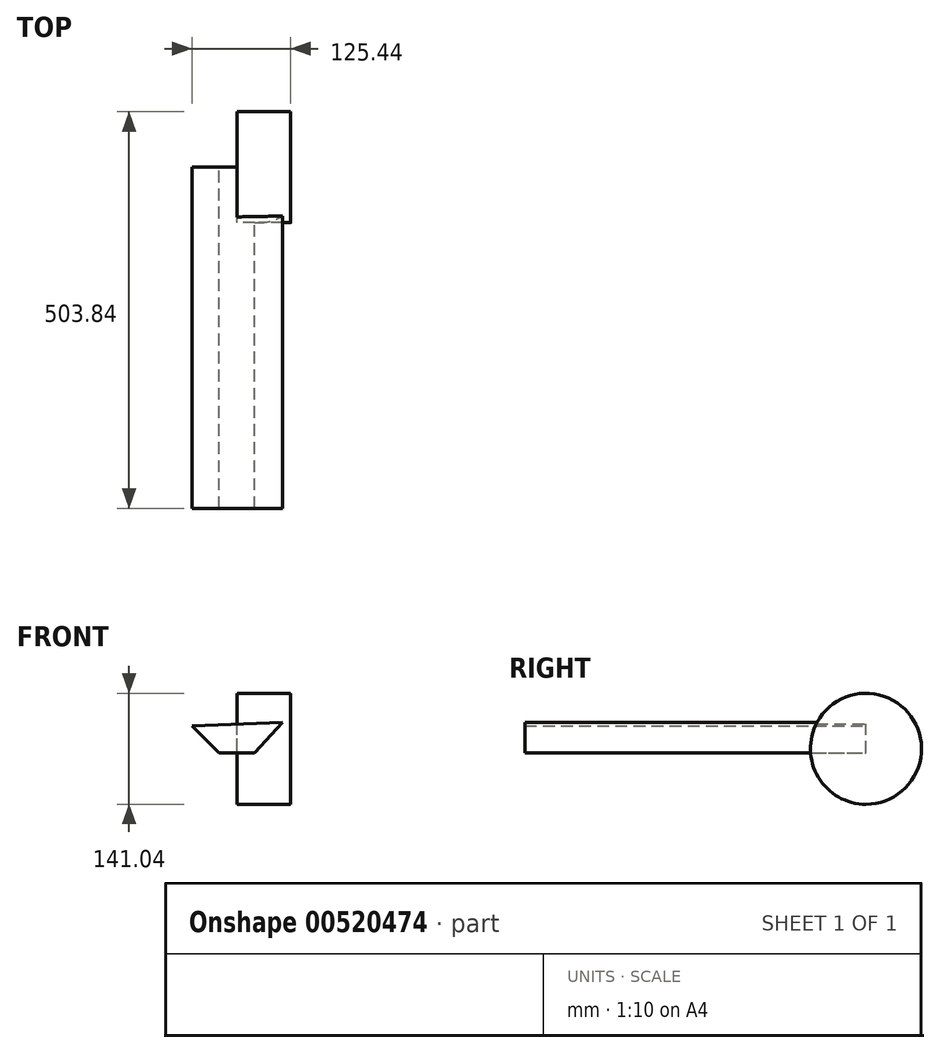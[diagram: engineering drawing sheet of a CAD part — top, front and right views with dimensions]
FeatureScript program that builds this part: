
annotation { "Feature Type Name" : "Feature", "Feature Type Description" : "" }
export const myFeature = defineFeature(function(context is Context, id is Id, definition is map)
    precondition{}
    {
        {
            var Q0;
            Q0=qCreatedBy(makeId("Front.planeOp"),FACE);
            var sketch = newSketch(context, id + "F0", { "sketchPlane" : qUnion([Q0])});
            skLineSegment(sketch, "E0", {"start": v(-23, 1.23) * mm, "end": v(22.4, 1.23) * mm});
            skLineSegment(sketch, "E1", {"start": v(22.4, 1.23) * mm, "end": v(57.98, 39.88) * mm});
            skLineSegment(sketch, "E2", {"start": v(57.98, 39.88) * mm, "end": v(22.4, 1.23) * mm});
            skLineSegment(sketch, "E3", {"start": v(-23, 1.23) * mm, "end": v(-57.37, 35.59) * mm});
            skLineSegment(sketch, "E4", {"start": v(-57.37, 35.59) * mm, "end": v(57.98, 39.88) * mm});
            skLineSegment(sketch, "E5", {"start": v(-18.02, 37.05) * mm, "end": v(0.3, 56.96) * mm});
            skPoint(sketch, "E5.endSnap0", {"position": v(0.3, 37.73) * mm});
            skLineSegment(sketch, "E6", {"start": v(0.3, 56.96) * mm, "end": v(18.85, 39.88) * mm});
            skSolve(sketch);
        }
        {
            var Q0;
            Q0 = qSketchRegion(id + "F0", true);
            extrude(context, id + "F1", {"entities" : qUnion([Q0]), "depth" : 433.32 * mm, "offsetDistance" : 25.4 * mm});
        }
        {
            var Q0;
            Q0=qCreatedBy(makeId("Right.planeOp"),FACE);
            var sketch = newSketch(context, id + "F2", { "sketchPlane" : qUnion([Q0])});
            skCircle(sketch, "E7", {"center": v(0, 6.36) * mm, "radius": 70.52 * mm});
            skSolve(sketch);
        }
        {
            var Q0;
            Q0 = qSketchRegion(id + "F2", true);
            extrude(context, id + "F3", {"entities" : qUnion([Q0]), "operationType" : NewBodyOperationType.ADD, "depth" : 68.07 * mm, "offsetDistance" : 25.4 * mm});
        }
    });
